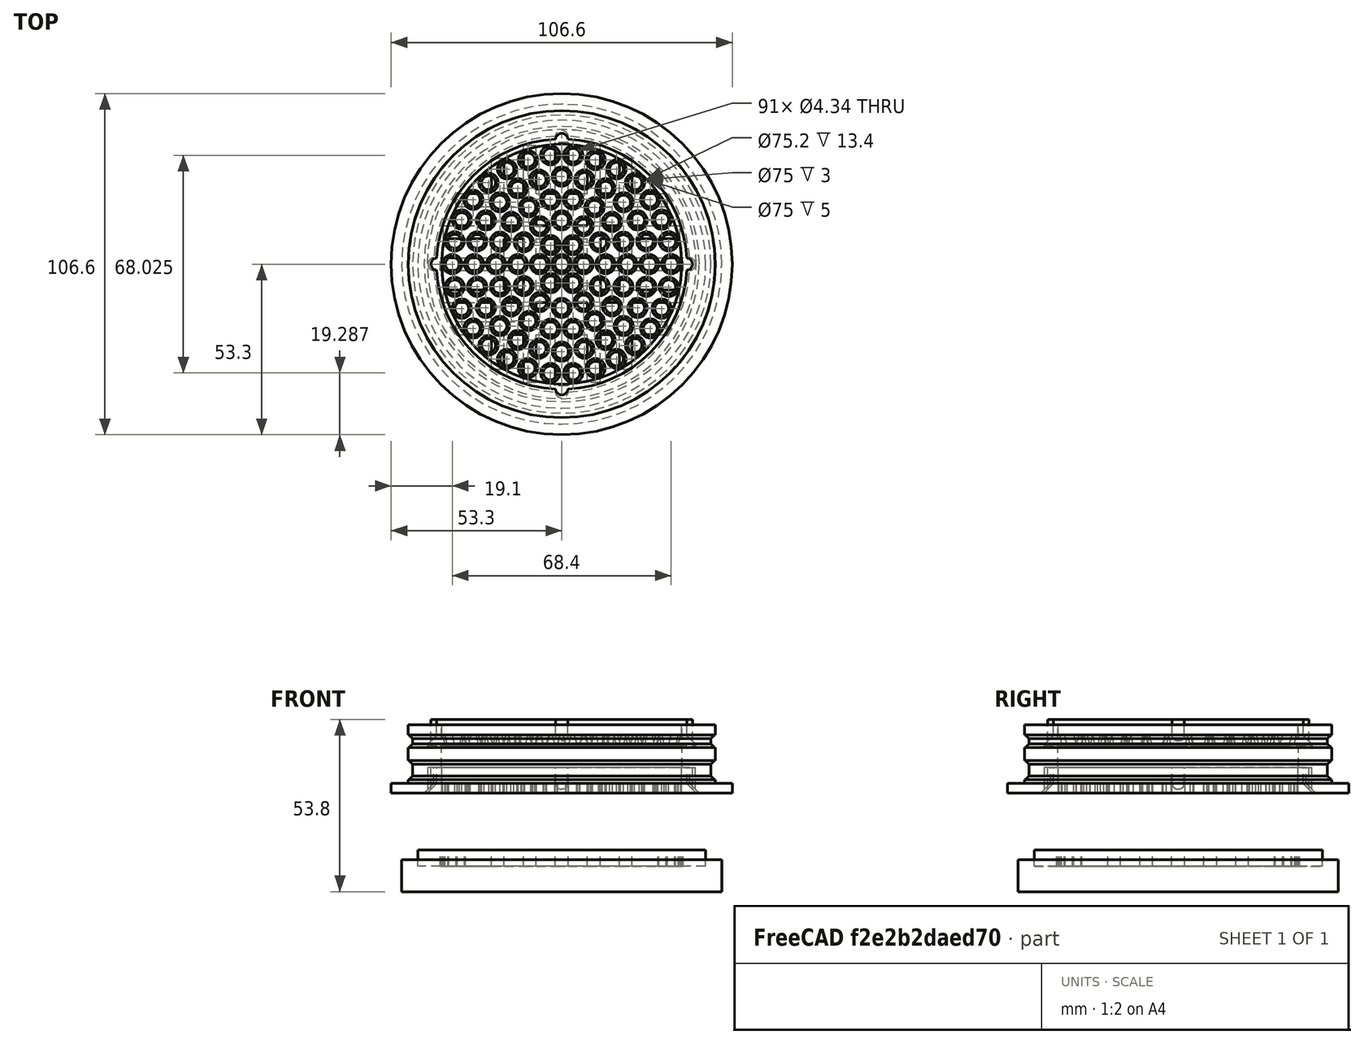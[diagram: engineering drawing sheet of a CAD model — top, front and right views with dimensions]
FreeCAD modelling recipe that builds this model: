
FCSTD DOCUMENT  (FreeCAD 0.18.4R)
Label: rejilla_v4
License: CreativeCommons Attribution-ShareAlike
LicenseURL: http://creativecommons.org/licenses/by-sa/4.0/
objects: Part::Cylinder×73, Part::Cut×34, Part::MultiFuse×21, Part::Box×20, Part::Cone×11, Part::FeaturePython×10, Part::Chamfer×2
note: 171 computed .brp shape members not serialized (recipe doc carries the construction recipe); baked Part::Feature solids carry a one-line shape summary decoded from their .brp

FEATURE [Part::Box] Box021  label="Cube021"
  AttacherType = Attacher::AttachEngine3D
  Height = 5
  Length = 66
  Placement = pos=(-33,18,-41) rot=(0,0,1;0rad)
  Width = 4
FEATURE [Part::Box] Box020  label="Cube020"
  AttacherType = Attacher::AttachEngine3D
  Height = 5
  Length = 74
  Placement = pos=(-37,8,-41) rot=(0,0,1;0rad)
  Width = 4
FEATURE [Part::Cylinder] Cylinder063
  Angle = 360
  AttacherType = Attacher::AttachEngine3D
  Height = 10
  Placement = pos=(0,0,-49) rot=(0,0,1;0rad)
  Radius = 50
FEATURE [Part::Box] Box023  label="Cube023"
  AttacherType = Attacher::AttachEngine3D
  Height = 5
  Length = 74
  Placement = pos=(12,-37,-41) rot=(0,0,1;1.5708rad)
  Width = 4
FEATURE [Part::Box] Box028  label="Cube028"
  AttacherType = Attacher::AttachEngine3D
  Height = 5
  Length = 66
  Placement = pos=(22,-33,-41) rot=(0,0,1;1.5708rad)
  Width = 4
FEATURE [Part::Cylinder] Cylinder060
  Angle = 360
  AttacherType = Attacher::AttachEngine3D
  Height = 5
  Placement = pos=(0,0,-41) rot=(0,0,1;0rad)
  Radius = 37.5
FEATURE [Part::Cylinder] Cylinder059
  Angle = 360
  AttacherType = Attacher::AttachEngine3D
  Height = 5
  Placement = pos=(0,0,-41) rot=(0,0,1;0rad)
  Radius = 45
FEATURE [Part::Box] Box025  label="Cube025"
  AttacherType = Attacher::AttachEngine3D
  Height = 5
  Length = 74
  Placement = pos=(-37,-12,-41) rot=(0,0,1;0rad)
  Width = 4
FEATURE [Part::Cone] Cone
  Angle = 360
  AttacherType = Attacher::AttachEngine3D
  Height = 5
  Placement = pos=(0,0,-15.2) rot=(0,1,0;3.14159rad)
  Radius1 = 40
  Radius2 = 45
FEATURE [Part::Cylinder] Cylinder072
  Angle = 360
  AttacherType = Attacher::AttachEngine3D
  Height = 3
  Radius = 47.3
FEATURE [Part::Cylinder] Cylinder073
  Angle = 360
  AttacherType = Attacher::AttachEngine3D
  Height = 7.8
  Placement = pos=(0,-39.8,-18) rot=(0,0,1;0rad)
  Radius = 2
FEATURE [Part::Box] Box024  label="Cube024"
  AttacherType = Attacher::AttachEngine3D
  Height = 5
  Length = 66
  Placement = pos=(-18,-33,-41) rot=(0,0,1;1.5708rad)
  Width = 4
FEATURE [Part::Cylinder] Cylinder056
  Angle = 360
  AttacherType = Attacher::AttachEngine3D
  Height = 13.4
  Placement = pos=(0,0,-10.2) rot=(0,0,1;0rad)
  Radius = 37.6
FEATURE [Part::Box] Box022  label="Cube022"
  AttacherType = Attacher::AttachEngine3D
  Height = 5
  Length = 74
  Placement = pos=(-8,-37,-41) rot=(0,0,1;1.5708rad)
  Width = 4
FEATURE [Part::Cylinder] Cylinder065
  Angle = 360
  AttacherType = Attacher::AttachEngine3D
  Height = 5
  Placement = pos=(0,0,-41) rot=(0,0,1;0rad)
  Radius = 37.3
FEATURE [Part::Cut] Cut035  label="anillo002"
  Base = -> Cylinder060
  Tool = -> Cylinder065
FEATURE [Part::Cylinder] Cylinder
  Angle = 360
  AttacherType = Attacher::AttachEngine3D
  Height = 3.2
  Radius = 48
FEATURE [Part::Cylinder] Cylinder071
  Angle = 360
  AttacherType = Attacher::AttachEngine3D
  Height = 3
  Radius = 53.3
FEATURE [Part::Cut] Cut037  label="extiende_rejilla_externa"
  Base = -> Cylinder071
  Placement = pos=(0,0,-18.2) rot=(0,0,1;0rad)
  Tool = -> Cylinder072
FEATURE [Part::Box] Box029  label="Cube029"
  AttacherType = Attacher::AttachEngine3D
  Height = 5
  Length = 76
  Placement = pos=(2,-38,-41) rot=(0,0,1;1.5708rad)
  Width = 4
FEATURE [Part::Cylinder] Cylinder067
  Angle = 360
  AttacherType = Attacher::AttachEngine3D
  Height = 5
  Placement = pos=(0,0,-41) rot=(0,0,1;0rad)
  Radius = 37.5
FEATURE [Part::Cut] Cut032
  Base = -> Cylinder059
  Tool = -> Cylinder067
FEATURE [Part::Cylinder] Cylinder009
  Angle = 360
  AttacherType = Attacher::AttachEngine3D
  Height = 27.4
  Placement = pos=(0,0,-17) rot=(0,0,1;0rad)
  Radius = 40
FEATURE [Part::MultiFuse] Fusion002
  Shapes = -> [Cylinder009,Cone]
FEATURE [Part::Cylinder] Cylinder002
  Angle = 360
  AttacherType = Attacher::AttachEngine3D
  Height = 4
  Placement = pos=(0,0,-8) rot=(0,0,1;0rad)
  Radius = 48
FEATURE [Part::Cylinder] Cylinder055
  Angle = 360
  AttacherType = Attacher::AttachEngine3D
  Height = 13.4
  Placement = pos=(0,0,-10.2) rot=(0,0,1;0rad)
  Radius = 40
FEATURE [Part::Cut] Cut026
  Base = -> Cylinder055
  Tool = -> Cylinder056
FEATURE [Part::Cylinder] Cylinder007
  Angle = 360
  AttacherType = Attacher::AttachEngine3D
  Height = 25
  Placement = pos=(0,0,-23) rot=(0,0,1;0rad)
  Radius = 45
FEATURE [Part::Box] Box027  label="Cube027"
  AttacherType = Attacher::AttachEngine3D
  Height = 5
  Length = 66
  Placement = pos=(-33,-22,-41) rot=(0,0,1;0rad)
  Width = 4
FEATURE [Part::Cylinder] Cylinder001
  Angle = 360
  AttacherType = Attacher::AttachEngine3D
  Height = 4
  Placement = pos=(0,0,-4) rot=(0,0,1;0rad)
  Radius = 46.6
FEATURE [Part::Cylinder] Cylinder005
  Angle = 360
  AttacherType = Attacher::AttachEngine3D
  Height = 25
  Placement = pos=(0,0,-18) rot=(0,0,1;0rad)
  Radius = 45
FEATURE [Part::Cylinder] Cylinder058
  Angle = 360
  AttacherType = Attacher::AttachEngine3D
  Height = 7.8
  Placement = pos=(-39.8,0,-18) rot=(0,0,1;0rad)
  Radius = 2
FEATURE [Part::Cylinder] Cylinder008
  Angle = 360
  AttacherType = Attacher::AttachEngine3D
  Height = 23.4
  Placement = pos=(0,0,-20.2) rot=(0,0,1;0rad)
  Radius = 45
FEATURE [Part::Cut] Cut002
  Base = -> Cylinder008
  Tool = -> Fusion002
FEATURE [Part::Cylinder] Cylinder019  label="ajustar_radio_de_este001"
  Angle = 360
  AttacherType = Attacher::AttachEngine3D
  Height = 5
  Placement = pos=(0,0,-23.2) rot=(0,0,1;0rad)
  Radius = 68.3
FEATURE [Part::Cylinder] Cylinder057
  Angle = 360
  AttacherType = Attacher::AttachEngine3D
  Height = 7.8
  Placement = pos=(39.8,0,-18) rot=(0,0,1;0rad)
  Radius = 2
FEATURE [Part::Cylinder] Cylinder006  label="ajustar_radio_de_este"
  Angle = 360
  AttacherType = Attacher::AttachEngine3D
  Height = 5
  Placement = pos=(0,0,-20.2) rot=(0,0,1;0rad)
  Radius = 51.3
FEATURE [Part::Cut] Cut001
  Base = -> Cylinder006
  Tool = -> Cylinder007
FEATURE [Part::Cylinder] Cylinder054
  Angle = 360
  AttacherType = Attacher::AttachEngine3D
  Height = 7.8
  Placement = pos=(0,39.8,-18) rot=(0,0,1;0rad)
  Radius = 2
FEATURE [Part::Cylinder] Cylinder004
  Angle = 360
  AttacherType = Attacher::AttachEngine3D
  Height = 1.2
  Placement = pos=(0,0,-15.2) rot=(0,0,1;0rad)
  Radius = 48
FEATURE [Part::Cylinder] Cylinder003
  Angle = 360
  AttacherType = Attacher::AttachEngine3D
  Height = 6
  Placement = pos=(0,0,-14) rot=(0,0,1;0rad)
  Radius = 46.6
FEATURE [Part::MultiFuse] Fusion
  Shapes = -> [Cylinder004,Cylinder,Cylinder003,Cylinder001,Cylinder002]
FEATURE [Part::Cut] Cut
  Base = -> Fusion
  Tool = -> Cylinder005
FEATURE [Part::MultiFuse] Fusion001
  Shapes = -> [Cut001,Cut]
FEATURE [Part::MultiFuse] Fusion003  label="rejilla_sin_cortar_oblicuo_sin_chaflan"
  Shapes = -> [Fusion001,Cut002]
FEATURE [Part::Chamfer] Chamfer
  Base = -> Fusion003
  Edges = 2 edges r=1.2: [Edge12,Edge24]
FEATURE [Part::Chamfer] Chamfer001  label="rejilla__exteriorsin_cortar_oblicuo_alta"
  Base = -> Chamfer
  Edges = 2 edges r=1.2: [Edge8,Edge26]
FEATURE [Part::Cut] Cut009  label="rejilla__exterior_sin_cortar_oblicuo_sin_muescas_01"
  Base = -> Chamfer001
  Tool = -> Cylinder019
FEATURE [Part::MultiFuse] Fusion019  label="rejilla__exterior_sin_cortar_oblicuo_sin_muescas"
  Shapes = -> [Cut009,Cut026]
FEATURE [Part::Cut] Cut027
  Base = -> Fusion019
  Tool = -> Cylinder054
FEATURE [Part::Cut] Cut028
  Base = -> Cut027
  Tool = -> Cylinder057
FEATURE [Part::Cut] Cut029  label="rejilla__exterior_sin_cortar_3_muescas"
  Base = -> Cut028
  Tool = -> Cylinder058
FEATURE [Part::Box] Box026  label="Cube026"
  AttacherType = Attacher::AttachEngine3D
  Height = 5
  Length = 76
  Placement = pos=(-38,-2,-41) rot=(0,0,1;0rad)
  Width = 4
FEATURE [Part::MultiFuse] Fusion022
  Shapes = -> [Cut035,Box024,Box028,Box022,Box020,Box025,Box027,Box026,Box021,Box029,Box023]
FEATURE [Part::Cut] Cut036  label="panal_version_1"
  Base = -> Fusion022
  Tool = -> Cut032
FEATURE [Part::Cut] Cut034  label="panal_version1"
  Base = -> Cut036
  Placement = pos=(0,0,20.8) rot=(0,0,1;0rad)
  Tool = -> Cylinder063
FEATURE [Part::Cut] Cut038  label="rejilla_externa_angosta"
  Base = -> Cut029
  Tool = -> Cylinder073
FEATURE [Part::MultiFuse] Fusion025  label="rejilla_externa"
  Shapes = -> [Cut038,Cut037]
FEATURE [Part::Cylinder] Cylinder066
  Angle = 360
  AttacherType = Attacher::AttachEngine3D
  Height = 32
  Placement = pos=(0,0,-39) rot=(0,0,1;0rad)
  Radius = 37.5
FEATURE [Part::Cylinder] Cylinder069  label="Cylinder_este_Es_el_mas_externo"
  Angle = 360
  AttacherType = Attacher::AttachEngine3D
  Height = 5
  Radius = 39.1
FEATURE [Part::Cylinder] Cylinder070
  Angle = 360
  AttacherType = Attacher::AttachEngine3D
  Height = 7.8
  Placement = pos=(38.95,0,-18) rot=(0,0,1;0rad)
  Radius = 1.9
FEATURE [Part::Cylinder] Cylinder064
  Angle = 360
  AttacherType = Attacher::AttachEngine3D
  Height = 5
  Radius = 37.5
FEATURE [Part::Cut] Cut033
  Base = -> Cylinder069
  Placement = pos=(0,0,-15.2) rot=(0,0,1;0rad)
  Tool = -> Cylinder064
FEATURE [Part::Cylinder] Cylinder061  label="ajustar_radio_de_este006"
  Angle = 360
  AttacherType = Attacher::AttachEngine3D
  Height = 5
  Placement = pos=(0,0,-23.2) rot=(0,0,1;0rad)
  Radius = 68.3
FEATURE [Part::Cylinder] Cylinder062
  Angle = 360
  AttacherType = Attacher::AttachEngine3D
  Height = 7.8
  Placement = pos=(0,38.95,-18) rot=(0,0,1;0rad)
  Radius = 1.9
FEATURE [Part::Cone] Cone004  label="Cone004_este_es_el_mas_externo"
  Angle = 360
  AttacherType = Attacher::AttachEngine3D
  Height = 5
  Placement = pos=(0,0,-15.2) rot=(0,1,0;3.14159rad)
  Radius1 = 39.1
  Radius2 = 44
FEATURE [Part::Cut] Cut030  label="cono_superior"
  Base = -> Cone004
  Tool = -> Cylinder066
FEATURE [Part::MultiFuse] Fusion020  label="rejilla_interior_sin_cortar_oblicuo_sin_tapa_007"
  Shapes = -> [Cut033,Cut030]
FEATURE [Part::Cut] Cut031  label="superior_sin_panal_sin_guias"
  Base = -> Fusion020
  Tool = -> Cylinder061
FEATURE [Part::Cylinder] Cylinder068
  Angle = 360
  AttacherType = Attacher::AttachEngine3D
  Height = 7.8
  Placement = pos=(-38.95,0,-18) rot=(0,0,1;0rad)
  Radius = 1.9
FEATURE [Part::Cylinder] Cylinder074
  Angle = 360
  AttacherType = Attacher::AttachEngine3D
  Height = 7.8
  Placement = pos=(0,-38.95,-18) rot=(0,0,1;0rad)
  Radius = 1.9
FEATURE [Part::MultiFuse] Fusion026  label="superior_sin_panal_rebarba"
  Shapes = -> [Cut031,Cylinder070,Cylinder068,Cylinder062,Cylinder074]
FEATURE [Part::Cylinder] Cylinder075
  Angle = 360
  AttacherType = Attacher::AttachEngine3D
  Height = 12
  Placement = pos=(0,0,-20) rot=(0,0,1;0rad)
  Radius = 37.5
FEATURE [Part::Cut] Cut039  label="base_superior_sin_panal"
  Base = -> Fusion026
  Tool = -> Cylinder075
FEATURE [Part::Cylinder] Cylinder076
  Angle = 360
  AttacherType = Attacher::AttachEngine3D
  Height = 7.8
  Placement = pos=(-38.95,0,-18) rot=(0,0,1;0rad)
  Radius = 1.9
FEATURE [Part::Cylinder] Cylinder077
  Angle = 360
  AttacherType = Attacher::AttachEngine3D
  Height = 12
  Placement = pos=(0,0,-20) rot=(0,0,1;0rad)
  Radius = 37.5
FEATURE [Part::Cylinder] Cylinder078  label="ajustar_radio_de_este007"
  Angle = 360
  AttacherType = Attacher::AttachEngine3D
  Height = 5
  Placement = pos=(0,0,-23.2) rot=(0,0,1;0rad)
  Radius = 68.3
FEATURE [Part::Cylinder] Cylinder079
  Angle = 360
  AttacherType = Attacher::AttachEngine3D
  Height = 7.8
  Placement = pos=(0,38.95,-18) rot=(0,0,1;0rad)
  Radius = 1.9
FEATURE [Part::Cylinder] Cylinder080  label="Cylinder_este_Es_el_mas_externo001"
  Angle = 360
  AttacherType = Attacher::AttachEngine3D
  Height = 5
  Radius = 39.1
FEATURE [Part::Cylinder] Cylinder081
  Angle = 360
  AttacherType = Attacher::AttachEngine3D
  Height = 7.8
  Placement = pos=(38.95,0,-18) rot=(0,0,1;0rad)
  Radius = 1.9
FEATURE [Part::Cylinder] Cylinder082
  Angle = 360
  AttacherType = Attacher::AttachEngine3D
  Height = 32
  Placement = pos=(0,0,-39) rot=(0,0,1;0rad)
  Radius = 37.5
FEATURE [Part::Cylinder] Cylinder083
  Angle = 360
  AttacherType = Attacher::AttachEngine3D
  Height = 5
  Radius = 37.5
FEATURE [Part::Cut] Cut040
  Base = -> Cylinder080
  Placement = pos=(0,0,-15.2) rot=(0,0,1;0rad)
  Tool = -> Cylinder083
FEATURE [Part::Cone] Cone005  label="Cone004_este_es_el_mas_externo001"
  Angle = 360
  AttacherType = Attacher::AttachEngine3D
  Height = 5
  Placement = pos=(0,0,-15.2) rot=(0,1,0;3.14159rad)
  Radius1 = 39.1
  Radius2 = 44
FEATURE [Part::Cut] Cut042  label="cono_superior001"
  Base = -> Cone005
  Tool = -> Cylinder082
FEATURE [Part::MultiFuse] Fusion027  label="rejilla_interior_sin_cortar_oblicuo_sin_tapa_008"
  Shapes = -> [Cut040,Cut042]
FEATURE [Part::Cut] Cut041  label="superior_sin_panal_sin_guias001"
  Base = -> Fusion027
  Tool = -> Cylinder078
FEATURE [Part::Cylinder] Cylinder084
  Angle = 360
  AttacherType = Attacher::AttachEngine3D
  Height = 7.8
  Placement = pos=(0,-38.95,-18) rot=(0,0,1;0rad)
  Radius = 1.9
FEATURE [Part::MultiFuse] Fusion028  label="superior_sin_panal_rebarba001"
  Shapes = -> [Cut041,Cylinder081,Cylinder076,Cylinder079,Cylinder084]
FEATURE [Part::Cut] Cut043  label="superior_sin_panal1"
  Base = -> Fusion028
  Tool = -> Cylinder077
FEATURE [Part::Box] Box030  label="Cube030"
  AttacherType = Attacher::AttachEngine3D
  Height = 5
  Length = 66
  Placement = pos=(-33,18,-41) rot=(0,0,1;0rad)
  Width = 4
FEATURE [Part::Cylinder] Cylinder085
  Angle = 360
  AttacherType = Attacher::AttachEngine3D
  Height = 5
  Placement = pos=(0,0,-41) rot=(0,0,1;0rad)
  Radius = 37.5
FEATURE [Part::Cylinder] Cylinder086
  Angle = 360
  AttacherType = Attacher::AttachEngine3D
  Height = 5
  Placement = pos=(0,0,-41) rot=(0,0,1;0rad)
  Radius = 37.3
FEATURE [Part::Box] Box031  label="Cube031"
  AttacherType = Attacher::AttachEngine3D
  Height = 5
  Length = 76
  Placement = pos=(2,-38,-41) rot=(0,0,1;1.5708rad)
  Width = 4
FEATURE [Part::Cylinder] Cylinder087
  Angle = 360
  AttacherType = Attacher::AttachEngine3D
  Height = 5
  Placement = pos=(0,0,-41) rot=(0,0,1;0rad)
  Radius = 37.5
FEATURE [Part::Cut] Cut044  label="anillo003"
  Base = -> Cylinder087
  Tool = -> Cylinder086
FEATURE [Part::Box] Box032  label="Cube032"
  AttacherType = Attacher::AttachEngine3D
  Height = 5
  Length = 74
  Placement = pos=(12,-37,-41) rot=(0,0,1;1.5708rad)
  Width = 4
FEATURE [Part::Cylinder] Cylinder088
  Angle = 360
  AttacherType = Attacher::AttachEngine3D
  Height = 5
  Placement = pos=(0,0,-41) rot=(0,0,1;0rad)
  Radius = 45
FEATURE [Part::Cut] Cut047
  Base = -> Cylinder088
  Tool = -> Cylinder085
FEATURE [Part::Box] Box033  label="Cube033"
  AttacherType = Attacher::AttachEngine3D
  Height = 5
  Length = 66
  Placement = pos=(-33,-22,-41) rot=(0,0,1;0rad)
  Width = 4
FEATURE [Part::Box] Box034  label="Cube034"
  AttacherType = Attacher::AttachEngine3D
  Height = 5
  Length = 66
  Placement = pos=(22,-33,-41) rot=(0,0,1;1.5708rad)
  Width = 4
FEATURE [Part::Cylinder] Cylinder089
  Angle = 360
  AttacherType = Attacher::AttachEngine3D
  Height = 10
  Placement = pos=(0,0,-49) rot=(0,0,1;0rad)
  Radius = 50
FEATURE [Part::Box] Box035  label="Cube035"
  AttacherType = Attacher::AttachEngine3D
  Height = 5
  Length = 74
  Placement = pos=(-37,-12,-41) rot=(0,0,1;0rad)
  Width = 4
FEATURE [Part::Box] Box036  label="Cube036"
  AttacherType = Attacher::AttachEngine3D
  Height = 5
  Length = 74
  Placement = pos=(-8,-37,-41) rot=(0,0,1;1.5708rad)
  Width = 4
FEATURE [Part::Box] Box037  label="Cube037"
  AttacherType = Attacher::AttachEngine3D
  Height = 5
  Length = 66
  Placement = pos=(-18,-33,-41) rot=(0,0,1;1.5708rad)
  Width = 4
FEATURE [Part::Box] Box038  label="Cube038"
  AttacherType = Attacher::AttachEngine3D
  Height = 5
  Length = 74
  Placement = pos=(-37,8,-41) rot=(0,0,1;0rad)
  Width = 4
FEATURE [Part::Box] Box039  label="Cube039"
  AttacherType = Attacher::AttachEngine3D
  Height = 5
  Length = 76
  Placement = pos=(-38,-2,-41) rot=(0,0,1;0rad)
  Width = 4
FEATURE [Part::MultiFuse] Fusion029
  Shapes = -> [Cut044,Box037,Box034,Box036,Box038,Box035,Box033,Box039,Box030,Box031,Box032]
FEATURE [Part::MultiFuse] Fusion030  label="rejilla_interior_panal1"
  Shapes = -> [Cut043,Cut034]
FEATURE [Part::Cylinder] Cylinder090
  Angle = 360
  AttacherType = Attacher::AttachEngine3D
  Height = 32
  Placement = pos=(0,0,-39) rot=(0,0,1;0rad)
  Radius = 37.5
FEATURE [Part::Cylinder] Cylinder091
  Angle = 360
  AttacherType = Attacher::AttachEngine3D
  Height = 7.8
  Placement = pos=(38.95,0,-18) rot=(0,0,1;0rad)
  Radius = 1.9
FEATURE [Part::Cylinder] Cylinder092
  Angle = 360
  AttacherType = Attacher::AttachEngine3D
  Height = 5
  Radius = 37.5
FEATURE [Part::Cylinder] Cylinder093  label="Cylinder_este_Es_el_mas_externo002"
  Angle = 360
  AttacherType = Attacher::AttachEngine3D
  Height = 5
  Radius = 39.1
FEATURE [Part::Cylinder] Cylinder094
  Angle = 360
  AttacherType = Attacher::AttachEngine3D
  Height = 12
  Placement = pos=(0,0,-20) rot=(0,0,1;0rad)
  Radius = 37.5
FEATURE [Part::Cylinder] Cylinder095  label="ajustar_radio_de_este008"
  Angle = 360
  AttacherType = Attacher::AttachEngine3D
  Height = 5
  Placement = pos=(0,0,-23.2) rot=(0,0,1;0rad)
  Radius = 68.3
FEATURE [Part::Cylinder] Cylinder096
  Angle = 360
  AttacherType = Attacher::AttachEngine3D
  Height = 7.8
  Placement = pos=(-38.95,0,-18) rot=(0,0,1;0rad)
  Radius = 1.9
FEATURE [Part::Cylinder] Cylinder097
  Angle = 360
  AttacherType = Attacher::AttachEngine3D
  Height = 7.8
  Placement = pos=(0,-38.95,-18) rot=(0,0,1;0rad)
  Radius = 1.9
FEATURE [Part::Cylinder] Cylinder098
  Angle = 360
  AttacherType = Attacher::AttachEngine3D
  Height = 7.8
  Placement = pos=(0,38.95,-18) rot=(0,0,1;0rad)
  Radius = 1.9
FEATURE [Part::Cone] Cone006  label="Cone004_este_es_el_mas_externo002"
  Angle = 360
  AttacherType = Attacher::AttachEngine3D
  Height = 5
  Placement = pos=(0,0,-15.2) rot=(0,1,0;3.14159rad)
  Radius1 = 39.1
  Radius2 = 44
FEATURE [Part::Cut] Cut049
  Base = -> Cylinder093
  Placement = pos=(0,0,-15.2) rot=(0,0,1;0rad)
  Tool = -> Cylinder092
FEATURE [Part::Cut] Cut050  label="cono_superior002"
  Base = -> Cone006
  Tool = -> Cylinder090
FEATURE [Part::MultiFuse] Fusion032  label="rejilla_interior_sin_cortar_oblicuo_sin_tapa_009"
  Shapes = -> [Cut049,Cut050]
FEATURE [Part::Cut] Cut051  label="superior_sin_panal_sin_guias002"
  Base = -> Fusion032
  Tool = -> Cylinder095
FEATURE [Part::MultiFuse] Fusion031  label="superior_sin_panal_rebarba002"
  Shapes = -> [Cut051,Cylinder091,Cylinder096,Cylinder098,Cylinder097]
FEATURE [Part::Cut] Cut048  label="base_superior_sin_panal2"
  Base = -> Fusion031
  Tool = -> Cylinder094
FEATURE [Part::Cylinder] Cylinder099
  Angle = 360
  AttacherType = Attacher::AttachEngine3D
  Height = 10
  Placement = pos=(0,0,-44) rot=(0,0,1;0rad)
  Radius = 2.17
FEATURE [Part::Cylinder] Cylinder100
  Angle = 360
  AttacherType = Attacher::AttachEngine3D
  Height = 10
  Placement = pos=(-6.84,0,-44) rot=(0,0,1;0rad)
  Radius = 2.17
FEATURE [Part::Cylinder] Cylinder101
  Angle = 360
  AttacherType = Attacher::AttachEngine3D
  Height = 10
  Placement = pos=(-20.52,0,-44) rot=(0,0,1;0rad)
  Radius = 2.17
FEATURE [Part::FeaturePython] Array  # Draft array (typed FeaturePython)
  Angle = 360
  ArrayType = 1
  Axis = (0,0,1)
  Base = -> Cylinder100
  Center = (0,0,0)
  Fuse = false
  IntervalAxis = (0,0,0)
  IntervalX = (1,0,0)
  IntervalY = (0,1,0)
  IntervalZ = (0,0,1)
  NumberPolar = 6
  NumberX = 2
  NumberY = 2
  NumberZ = 1
FEATURE [Part::Cylinder] Cylinder102
  Angle = 360
  AttacherType = Attacher::AttachEngine3D
  Height = 10
  Placement = pos=(-13.68,0,-44) rot=(0,0,1;0rad)
  Radius = 2.17
FEATURE [Part::FeaturePython] Array001  # Draft array (typed FeaturePython)
  Angle = 360
  ArrayType = 1
  Axis = (0,0,1)
  Base = -> Cylinder102
  Center = (0,0,0)
  Fuse = false
  IntervalAxis = (0,0,0)
  IntervalX = (1,0,0)
  IntervalY = (0,1,0)
  IntervalZ = (0,0,1)
  NumberPolar = 12
  NumberX = 2
  NumberY = 2
  NumberZ = 1
FEATURE [Part::FeaturePython] Array002  # Draft array (typed FeaturePython)
  Angle = 360
  ArrayType = 1
  Axis = (0,0,1)
  Base = -> Cylinder101
  Center = (0,0,0)
  Fuse = false
  IntervalAxis = (0,0,0)
  IntervalX = (1,0,0)
  IntervalY = (0,1,0)
  IntervalZ = (0,0,1)
  NumberPolar = 18
  NumberX = 2
  NumberY = 2
  NumberZ = 1
FEATURE [Part::Cylinder] Cylinder103
  Angle = 360
  AttacherType = Attacher::AttachEngine3D
  Height = 10
  Placement = pos=(-27.36,0,-44) rot=(0,0,1;0rad)
  Radius = 2.17
FEATURE [Part::Cylinder] Cylinder104
  Angle = 360
  AttacherType = Attacher::AttachEngine3D
  Height = 10
  Placement = pos=(-34.2,0,-44) rot=(0,0,1;0rad)
  Radius = 2.17
FEATURE [Part::FeaturePython] Array003  # Draft array (typed FeaturePython)
  Angle = 360
  ArrayType = 1
  Axis = (0,0,1)
  Base = -> Cylinder103
  Center = (0,0,0)
  Fuse = false
  IntervalAxis = (0,0,0)
  IntervalX = (1,0,0)
  IntervalY = (0,1,0)
  IntervalZ = (0,0,1)
  NumberPolar = 24
  NumberX = 2
  NumberY = 2
  NumberZ = 1
FEATURE [Part::FeaturePython] Array004  # Draft array (typed FeaturePython)
  Angle = 360
  ArrayType = 1
  Axis = (0,0,1)
  Base = -> Cylinder104
  Center = (0,0,0)
  Fuse = false
  IntervalAxis = (0,0,0)
  IntervalX = (1,0,0)
  IntervalY = (0,1,0)
  IntervalZ = (0,0,1)
  NumberPolar = 30
  NumberX = 2
  NumberY = 2
  NumberZ = 1
FEATURE [Part::Cylinder] Cylinder105
  Angle = 360
  AttacherType = Attacher::AttachEngine3D
  Height = 3
  Placement = pos=(0,0,-41) rot=(0,0,1;0rad)
  Radius = 38
FEATURE [Part::MultiFuse] Fusion033
  Shapes = -> [Array004,Array,Array003,Array001,Array002,Cylinder099]
FEATURE [Part::Cut] Cut052  label="panal2"
  Base = -> Cylinder105
  Placement = pos=(0,0,22.8) rot=(0,0,1;0rad)
  Tool = -> Fusion033
FEATURE [Part::MultiFuse] Fusion034  label="rejilla_interior_panal2"
  Shapes = -> [Cut048,Cut052]
FEATURE [Part::Cone] Cone007  label="Cone001"
  Angle = 360
  AttacherType = Attacher::AttachEngine3D
  Height = 3
  Radius1 = 3
  Radius2 = 2.17
FEATURE [Part::Cone] Cone008  label="Cone002"
  Angle = 360
  AttacherType = Attacher::AttachEngine3D
  Height = 3
  Placement = pos=(-6.84,0,0) rot=(0,0,1;0rad)
  Radius1 = 3
  Radius2 = 2.17
FEATURE [Part::Cylinder] Cylinder106
  Angle = 360
  AttacherType = Attacher::AttachEngine3D
  Height = 3
  Radius = 38
FEATURE [Part::Cone] Cone009  label="Cone003"
  Angle = 360
  AttacherType = Attacher::AttachEngine3D
  Height = 3
  Placement = pos=(-13.68,0,0) rot=(0,0,1;0rad)
  Radius1 = 3
  Radius2 = 2.17
FEATURE [Part::Cone] Cone010  label="Cone004"
  Angle = 360
  AttacherType = Attacher::AttachEngine3D
  Height = 3
  Placement = pos=(-20.52,0,0) rot=(0,0,1;0rad)
  Radius1 = 3
  Radius2 = 2.17
FEATURE [Part::Cone] Cone011  label="Cone005"
  Angle = 360
  AttacherType = Attacher::AttachEngine3D
  Height = 3
  Placement = pos=(-27.36,0,0) rot=(0,0,1;0rad)
  Radius1 = 3
  Radius2 = 2.17
FEATURE [Part::Cone] Cone012  label="Cone006"
  Angle = 360
  AttacherType = Attacher::AttachEngine3D
  Height = 3
  Placement = pos=(-34.2,0,0) rot=(0,0,1;0rad)
  Radius1 = 3
  Radius2 = 2.17
FEATURE [Part::FeaturePython] Array005  # Draft array (typed FeaturePython)
  Angle = 360
  ArrayType = 1
  Axis = (0,0,1)
  Base = -> Cone008
  Center = (0,0,0)
  Fuse = false
  IntervalAxis = (0,0,0)
  IntervalX = (1,0,0)
  IntervalY = (0,1,0)
  IntervalZ = (0,0,1)
  NumberPolar = 6
  NumberX = 2
  NumberY = 2
  NumberZ = 1
FEATURE [Part::FeaturePython] Array006  # Draft array (typed FeaturePython)
  Angle = 360
  ArrayType = 1
  Axis = (0,0,1)
  Base = -> Cone009
  Center = (0,0,0)
  Fuse = false
  IntervalAxis = (0,0,0)
  IntervalX = (1,0,0)
  IntervalY = (0,1,0)
  IntervalZ = (0,0,1)
  NumberPolar = 12
  NumberX = 2
  NumberY = 2
  NumberZ = 1
FEATURE [Part::FeaturePython] Array007  # Draft array (typed FeaturePython)
  Angle = 360
  ArrayType = 1
  Axis = (0,0,1)
  Base = -> Cone010
  Center = (0,0,0)
  Fuse = false
  IntervalAxis = (0,0,0)
  IntervalX = (1,0,0)
  IntervalY = (0,1,0)
  IntervalZ = (0,0,1)
  NumberPolar = 18
  NumberX = 2
  NumberY = 2
  NumberZ = 1
FEATURE [Part::FeaturePython] Array008  # Draft array (typed FeaturePython)
  Angle = 360
  ArrayType = 1
  Axis = (0,0,1)
  Base = -> Cone011
  Center = (0,0,0)
  Fuse = false
  IntervalAxis = (0,0,0)
  IntervalX = (1,0,0)
  IntervalY = (0,1,0)
  IntervalZ = (0,0,1)
  NumberPolar = 24
  NumberX = 2
  NumberY = 2
  NumberZ = 1
FEATURE [Part::FeaturePython] Array009  # Draft array (typed FeaturePython)
  Angle = 360
  ArrayType = 1
  Axis = (0,0,1)
  Base = -> Cone012
  Center = (0,0,0)
  Fuse = false
  IntervalAxis = (0,0,0)
  IntervalX = (1,0,0)
  IntervalY = (0,1,0)
  IntervalZ = (0,0,1)
  NumberPolar = 30
  NumberX = 2
  NumberY = 2
  NumberZ = 1
FEATURE [Part::MultiFuse] Fusion035
  Shapes = -> [Cone007,Array005,Array006,Array007,Array008,Array009]
FEATURE [Part::Cut] Cut053  label="panal2_v2"
  Base = -> Cylinder106
  Placement = pos=(0,0,-0.2) rot=(0,1,0;3.14159rad)
  Tool = -> Fusion035
FEATURE [Part::Cylinder] Cylinder107
  Angle = 360
  AttacherType = Attacher::AttachEngine3D
  Height = 32
  Placement = pos=(0,0,-39) rot=(0,0,1;0rad)
  Radius = 37.5
FEATURE [Part::Cylinder] Cylinder108
  Angle = 360
  AttacherType = Attacher::AttachEngine3D
  Height = 5
  Radius = 37.5
FEATURE [Part::Cylinder] Cylinder109
  Angle = 360
  AttacherType = Attacher::AttachEngine3D
  Height = 7.8
  Placement = pos=(38.95,0,-18) rot=(0,0,1;0rad)
  Radius = 1.9
FEATURE [Part::Cylinder] Cylinder110
  Angle = 360
  AttacherType = Attacher::AttachEngine3D
  Height = 7.8
  Placement = pos=(0,38.95,-18) rot=(0,0,1;0rad)
  Radius = 1.9
FEATURE [Part::Cylinder] Cylinder111  label="ajustar_radio_de_este009"
  Angle = 360
  AttacherType = Attacher::AttachEngine3D
  Height = 5
  Placement = pos=(0,0,-23.2) rot=(0,0,1;0rad)
  Radius = 68.3
FEATURE [Part::Cylinder] Cylinder112
  Angle = 360
  AttacherType = Attacher::AttachEngine3D
  Height = 7.8
  Placement = pos=(-38.95,0,-18) rot=(0,0,1;0rad)
  Radius = 1.9
FEATURE [Part::Cylinder] Cylinder113  label="Cylinder_este_Es_el_mas_externo003"
  Angle = 360
  AttacherType = Attacher::AttachEngine3D
  Height = 5
  Radius = 39.1
FEATURE [Part::Cut] Cut057
  Base = -> Cylinder113
  Placement = pos=(0,0,-15.2) rot=(0,0,1;0rad)
  Tool = -> Cylinder108
FEATURE [Part::Cylinder] Cylinder114
  Angle = 360
  AttacherType = Attacher::AttachEngine3D
  Height = 7.8
  Placement = pos=(0,-38.95,-18) rot=(0,0,1;0rad)
  Radius = 1.9
FEATURE [Part::Cylinder] Cylinder115
  Angle = 360
  AttacherType = Attacher::AttachEngine3D
  Height = 12
  Placement = pos=(0,0,-20) rot=(0,0,1;0rad)
  Radius = 37.5
FEATURE [Part::Cone] Cone013  label="Cone004_este_es_el_mas_externo003"
  Angle = 360
  AttacherType = Attacher::AttachEngine3D
  Height = 5
  Placement = pos=(0,0,-15.2) rot=(0,1,0;3.14159rad)
  Radius1 = 39.1
  Radius2 = 44
FEATURE [Part::Cut] Cut055  label="cono_superior003"
  Base = -> Cone013
  Tool = -> Cylinder107
FEATURE [Part::MultiFuse] Fusion036  label="rejilla_interior_sin_cortar_oblicuo_sin_tapa_010"
  Shapes = -> [Cut057,Cut055]
FEATURE [Part::Cut] Cut056  label="superior_sin_panal_sin_guias003"
  Base = -> Fusion036
  Tool = -> Cylinder111
FEATURE [Part::MultiFuse] Fusion037  label="superior_sin_panal_rebarba003"
  Shapes = -> [Cut056,Cylinder109,Cylinder112,Cylinder110,Cylinder114]
FEATURE [Part::Cut] Cut054  label="base_superior_para_panal2v2"
  Base = -> Fusion037
  Placement = pos=(0,0,15) rot=(0,0,1;0rad)
  Tool = -> Cylinder115
FEATURE [Part::MultiFuse] Fusion038  label="rejilla_interior_panal2v2"
  Shapes = -> [Cut053,Cut054]
